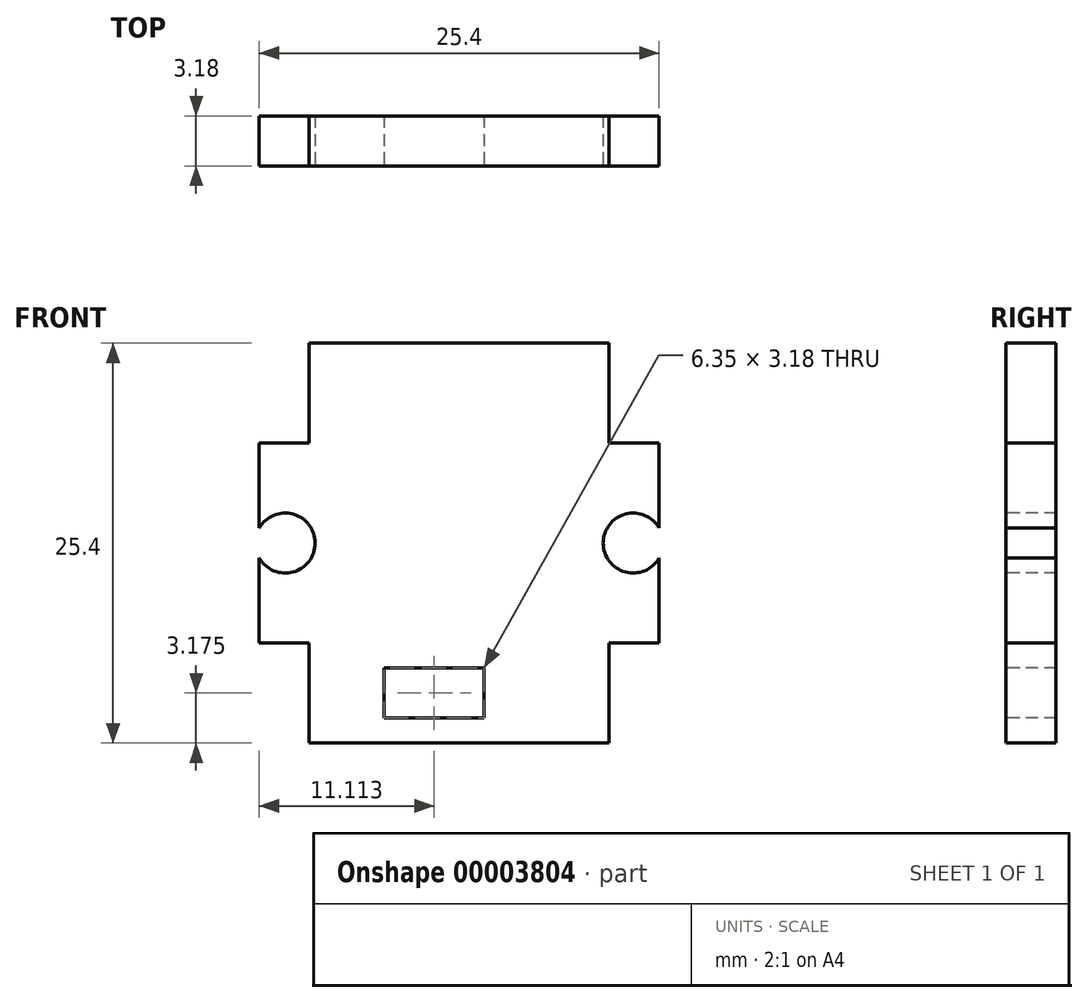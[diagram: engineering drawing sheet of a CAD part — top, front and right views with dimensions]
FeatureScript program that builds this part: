
annotation { "Feature Type Name" : "Feature", "Feature Type Description" : "" }
export const myFeature = defineFeature(function(context is Context, id is Id, definition is map)
    precondition{}
    {
        {
            var Q0;
            Q0=qCreatedBy(makeId("Front.planeOp"),FACE);
            var sketch = newSketch(context, id + "F0", { "sketchPlane" : qUnion([Q0])});
            skLineSegment(sketch, "E0.bottom", {"start": v(0, 0) * mm, "end": v(25.4, 0) * mm});
            skLineSegment(sketch, "E0.top", {"start": v(0, 25.4) * mm, "end": v(25.4, 25.4) * mm});
            skLineSegment(sketch, "E0.left", {"start": v(0, 0) * mm, "end": v(0, 25.4) * mm});
            skLineSegment(sketch, "E0.right", {"start": v(25.4, 0) * mm, "end": v(25.4, 25.4) * mm});
            skSolve(sketch);
        }
        {
            var Q0;
            Q0=makeQuery(id+"F0.imprint","IMPRINT",FACE,{"disambiguationData":[TD([[makeQuery(id+"F0.imprint","IMPRINT",EDGE,{"derivedFrom":sQuery(id+"F0.wireOp",EDGE,"E0.bottom")}),1.0]])]});
            var sketch = newSketch(context, id + "F1", { "sketchPlane" : qUnion([Q0])});
            skLineSegment(sketch, "E1.bottom", {"start": v(0, 0) * mm, "end": v(3.18, 0) * mm});
            skLineSegment(sketch, "E1.top", {"start": v(0, 6.35) * mm, "end": v(3.18, 6.35) * mm});
            skLineSegment(sketch, "E1.left", {"start": v(0, 0) * mm, "end": v(0, 6.35) * mm});
            skLineSegment(sketch, "E1.right", {"start": v(3.18, 0) * mm, "end": v(3.18, 6.35) * mm});
            skLineSegment(sketch, "E2", {"start": v(12.7, 50.73) * mm, "end": v(12.7, 0) * mm, "construction": true});
            skLineSegment(sketch, "E3", {"start": v(0, 12.7) * mm, "end": v(50.46, 12.7) * mm, "construction": true});
            skLineSegment(sketch, "E4.0.MirrorCS", {"start": v(25.4, 6.35) * mm, "end": v(22.23, 6.35) * mm});
            skLineSegment(sketch, "E5.0.MirrorCS", {"start": v(22.23, 0) * mm, "end": v(22.23, 6.35) * mm});
            skLineSegment(sketch, "E6.0.MirrorCS", {"start": v(25.4, 0) * mm, "end": v(22.23, 0) * mm});
            skLineSegment(sketch, "E7.0.MirrorCS", {"start": v(25.4, 0) * mm, "end": v(25.4, 6.35) * mm});
            skLineSegment(sketch, "E8.0.MirrorCS", {"start": v(0, 19.05) * mm, "end": v(3.18, 19.05) * mm});
            skLineSegment(sketch, "E9.0.MirrorCS", {"start": v(3.18, 25.4) * mm, "end": v(3.18, 19.05) * mm});
            skLineSegment(sketch, "E10.0.MirrorCS", {"start": v(0, 25.4) * mm, "end": v(3.18, 25.4) * mm});
            skLineSegment(sketch, "E11.0.MirrorCS", {"start": v(0, 25.4) * mm, "end": v(0, 19.05) * mm});
            skLineSegment(sketch, "E12.0.MirrorCS", {"start": v(22.23, 25.4) * mm, "end": v(22.23, 19.05) * mm});
            skLineSegment(sketch, "E13.0.MirrorCS", {"start": v(25.4, 25.4) * mm, "end": v(22.23, 25.4) * mm});
            skLineSegment(sketch, "E14.0.MirrorCS", {"start": v(25.4, 25.4) * mm, "end": v(25.4, 19.05) * mm});
            skLineSegment(sketch, "E15.0.MirrorCS", {"start": v(25.4, 19.05) * mm, "end": v(22.23, 19.05) * mm});
            skSolve(sketch);
        }
        {
            var Q0;
            Q0 = qSketchRegion(id + "F0", true);
            extrude(context, id + "F2", {"entities" : qUnion([Q0]), "oppositeDirection" : true, "depth" : 3.17 * mm});
        }
        {
            var Q0;
            Q0 = qSketchRegion(id + "F1", true);
            var Q1;
            Q1 = qSketchRegion(id + "FJ1jgFQQGefKnKE_1", true);
            extrude(context, id + "F3", {"entities" : qUnion([Q0, Q1]), "operationType" : NewBodyOperationType.REMOVE, "oppositeDirection" : true, "depth" : 3.17 * mm});
        }
        {
            var Q0;
            Q0=makeQuery(id+"F2.opExtrude","CAP_FACE",FACE,{"disambiguationData":[OSD([sQuery(id+"F0.wireOp",EDGE,"E0.bottom"),sQuery(id+"F0.wireOp",EDGE,"E0.top"),sQuery(id+"F0.wireOp",EDGE,"E0.left"),sQuery(id+"F0.wireOp",EDGE,"E0.right")])],"isStart":true});
            var sketch = newSketch(context, id + "F4", { "sketchPlane" : qUnion([Q0])});
            skLineSegment(sketch, "E16.bottom", {"start": v(7.94, 1.59) * mm, "end": v(14.29, 1.59) * mm});
            skLineSegment(sketch, "E16.top", {"start": v(7.94, 4.76) * mm, "end": v(14.29, 4.76) * mm});
            skLineSegment(sketch, "E16.left", {"start": v(7.94, 1.59) * mm, "end": v(7.94, 4.76) * mm});
            skLineSegment(sketch, "E16.right", {"start": v(14.29, 1.59) * mm, "end": v(14.29, 4.76) * mm});
            skSolve(sketch);
        }
        {
            var Q0;
            Q0 = qSketchRegion(id + "F4", true);
            extrude(context, id + "F5", {"entities" : qUnion([Q0]), "operationType" : NewBodyOperationType.REMOVE, "oppositeDirection" : true, "depth" : 3.17 * mm});
        }
        {
            var Q0;
            Q0=makeQuery(id+"F2.opExtrude","CAP_FACE",FACE,{"disambiguationData":[OSD([sQuery(id+"F0.wireOp",EDGE,"E0.bottom"),sQuery(id+"F0.wireOp",EDGE,"E0.top"),sQuery(id+"F0.wireOp",EDGE,"E0.left"),sQuery(id+"F0.wireOp",EDGE,"E0.right")])],"isStart":true});
            var sketch = newSketch(context, id + "F6", { "sketchPlane" : qUnion([Q0])});
            skArc(sketch, "E17", {"start": v(0, 11.75) * mm, "mid": v(3.55, 12.7) * mm, "end": v(0, 13.65) * mm});
            skLineSegment(sketch, "E18", {"start": v(12.7, 25.4) * mm, "end": v(12.7, 0) * mm, "construction": true});
            skArc(sketch, "E19.0.MirrorCS", {"start": v(25.4, 11.75) * mm, "mid": v(21.85, 12.7) * mm, "end": v(25.4, 13.65) * mm});
            skLineSegment(sketch, "E20", {"start": v(0, 13.65) * mm, "end": v(0, 11.75) * mm});
            skLineSegment(sketch, "E21", {"start": v(25.4, 11.75) * mm, "end": v(25.4, 13.65) * mm});
            skSolve(sketch);
        }
        {
            var Q0;
            Q0 = qSketchRegion(id + "F6", true);
            extrude(context, id + "F7", {"entities" : qUnion([Q0]), "operationType" : NewBodyOperationType.REMOVE, "oppositeDirection" : true, "depth" : 25.4 * mm});
        }
    });
